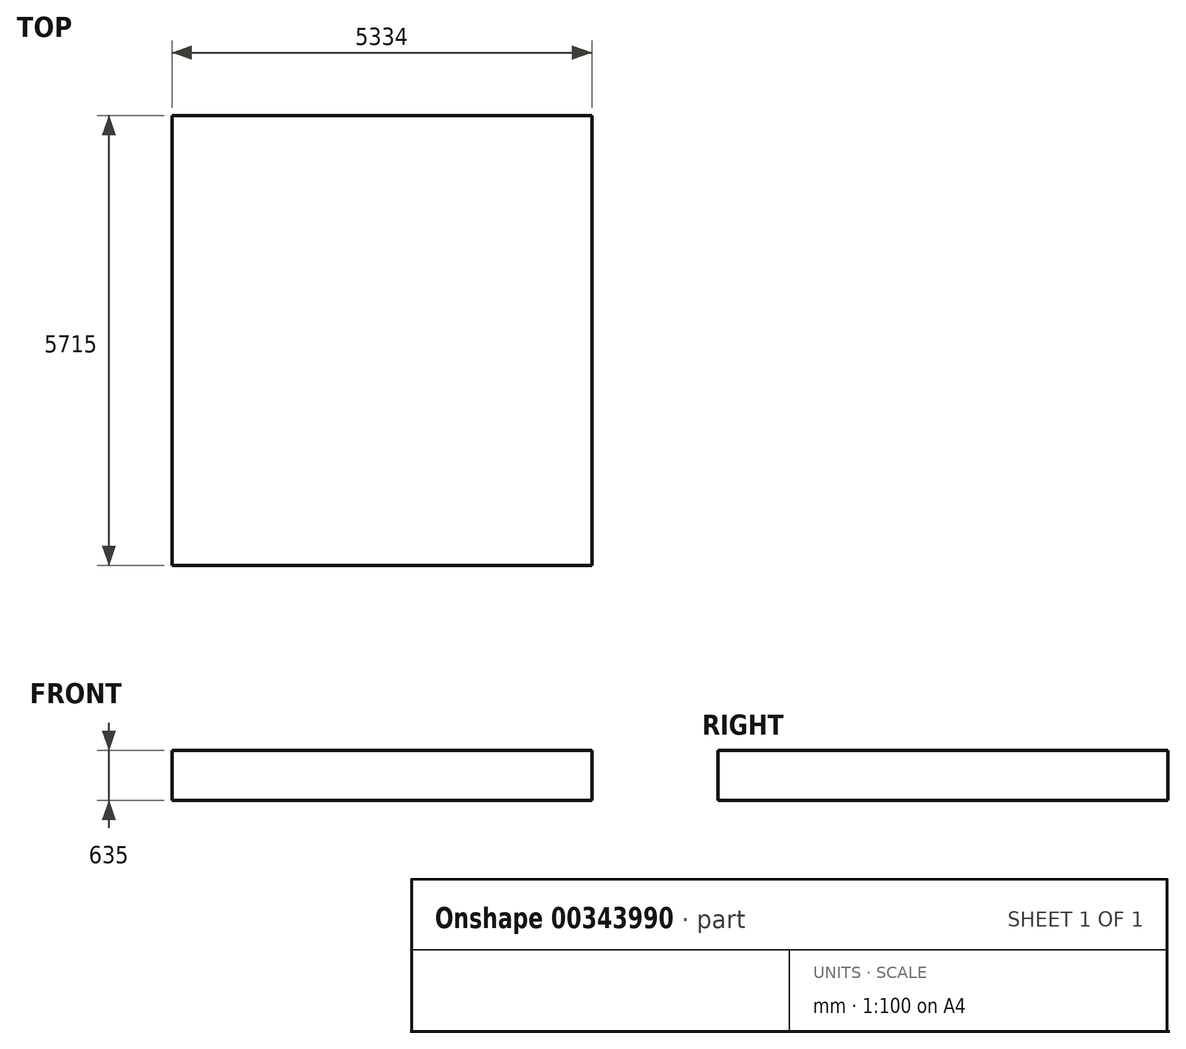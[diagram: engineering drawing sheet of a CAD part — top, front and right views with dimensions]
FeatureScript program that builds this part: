
annotation { "Feature Type Name" : "Feature", "Feature Type Description" : "" }
export const myFeature = defineFeature(function(context is Context, id is Id, definition is map)
    precondition{}
    {
        {
            var Q0;
            Q0=qCreatedBy(makeId("Top.planeOp"),FACE);
            var sketch = newSketch(context, id + "F0", { "sketchPlane" : qUnion([Q0])});
            skLineSegment(sketch, "E0.bottom", {"start": v(2667, -2857.5) * mm, "end": v(-2667, -2857.5) * mm});
            skLineSegment(sketch, "E0.top", {"start": v(2667, 2857.5) * mm, "end": v(-2667, 2857.5) * mm});
            skLineSegment(sketch, "E0.left", {"start": v(2667, -2857.5) * mm, "end": v(2667, 2857.5) * mm});
            skLineSegment(sketch, "E0.right", {"start": v(-2667, -2857.5) * mm, "end": v(-2667, 2857.5) * mm});
            skPoint(sketch, "E0.middle", {"position": v(0, 0) * mm});
            skSolve(sketch);
        }
        {
            var Q0;
            Q0=makeQuery(id+"F0.imprint","IMPRINT",FACE,{"disambiguationData":[TD([[makeQuery(id+"F0.imprint","IMPRINT",EDGE,{"derivedFrom":sQuery(id+"F0.wireOp",EDGE,"E0.bottom")}),-1.0]])]});
            extrude(context, id + "F1", {"entities" : qUnion([Q0]), "depth" : 635 * mm});
        }
    });
